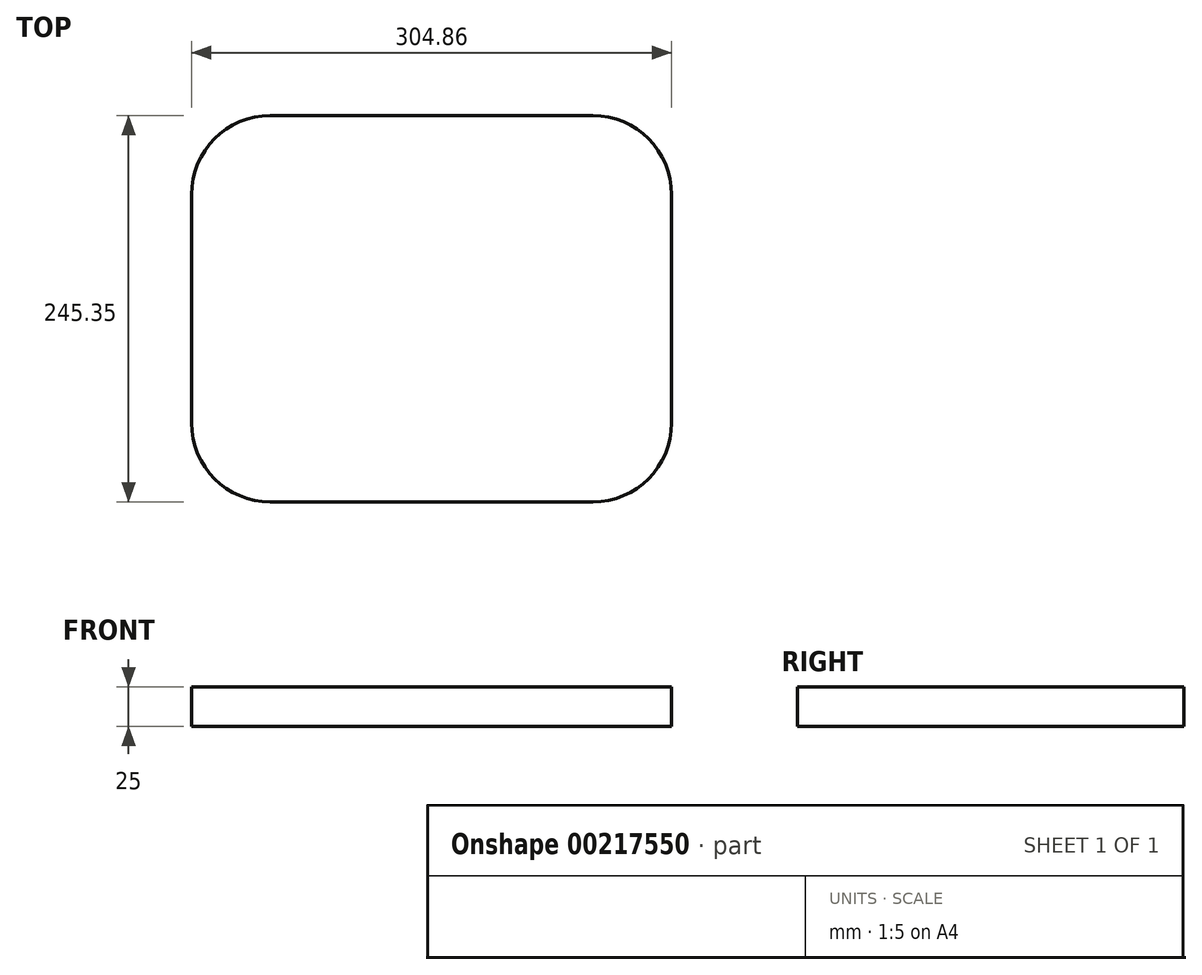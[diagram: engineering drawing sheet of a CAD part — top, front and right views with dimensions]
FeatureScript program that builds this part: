
annotation { "Feature Type Name" : "Feature", "Feature Type Description" : "" }
export const myFeature = defineFeature(function(context is Context, id is Id, definition is map)
    precondition{}
    {
        {
            var Q0;
            Q0=qCreatedBy(makeId("Top.planeOp"),FACE);
            var sketch = newSketch(context, id + "F0", { "sketchPlane" : qUnion([Q0])});
            skLineSegment(sketch, "E0.bottom", {"start": v(-118.4, 176.13) * mm, "end": v(86.45, 176.13) * mm});
            skLineSegment(sketch, "E0.top", {"start": v(-118.4, -69.22) * mm, "end": v(86.45, -69.22) * mm});
            skLineSegment(sketch, "E0.left", {"start": v(-168.4, 126.13) * mm, "end": v(-168.4, -19.22) * mm});
            skLineSegment(sketch, "E0.right", {"start": v(136.45, 126.13) * mm, "end": v(136.45, -19.22) * mm});
            skPoint(sketch, "E1.visualSharp", {"position": v(136.45, 176.13) * mm});
            skArc(sketch, "E1.filletArc", {"start": v(136.45, 126.13) * mm, "mid": v(121.8, 161.48) * mm, "end": v(86.45, 176.13) * mm});
            skPoint(sketch, "E2.visualSharp", {"position": v(-168.4, 176.13) * mm});
            skArc(sketch, "E2.filletArc", {"start": v(-118.4, 176.13) * mm, "mid": v(-153.76, 161.48) * mm, "end": v(-168.4, 126.13) * mm});
            skPoint(sketch, "E3.visualSharp", {"position": v(-168.4, -69.22) * mm});
            skArc(sketch, "E3.filletArc", {"start": v(-168.4, -19.22) * mm, "mid": v(-153.76, -54.57) * mm, "end": v(-118.4, -69.22) * mm});
            skPoint(sketch, "E4.visualSharp", {"position": v(136.45, -69.22) * mm});
            skArc(sketch, "E4.filletArc", {"start": v(86.45, -69.22) * mm, "mid": v(121.8, -54.57) * mm, "end": v(136.45, -19.22) * mm});
            skSolve(sketch);
        }
        {
            var Q0;
            Q0=makeQuery(id+"F0.imprint","IMPRINT",FACE,{"disambiguationData":[TD([[makeQuery(id+"F0.imprint","IMPRINT",EDGE,{"derivedFrom":sQuery(id+"F0.wireOp",EDGE,"E0.bottom")}),-1.0]])]});
            extrude(context, id + "F1", {"entities" : qUnion([Q0]), "depth" : 25 * mm});
        }
    });
